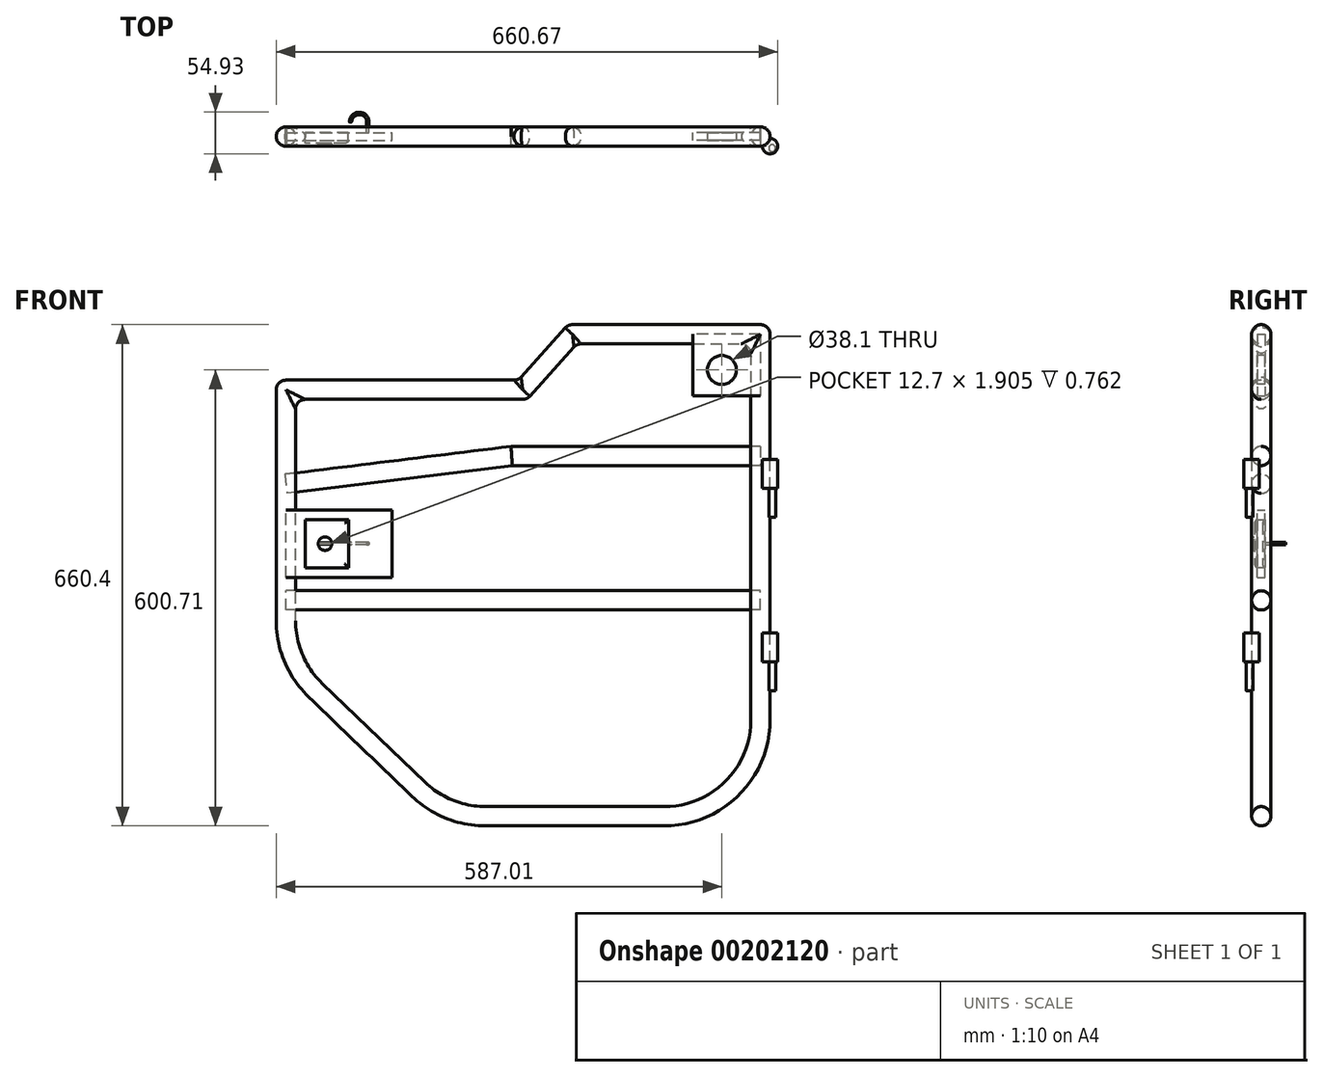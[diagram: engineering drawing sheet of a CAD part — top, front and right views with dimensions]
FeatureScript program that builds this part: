
annotation { "Feature Type Name" : "Feature", "Feature Type Description" : "" }
export const myFeature = defineFeature(function(context is Context, id is Id, definition is map)
    precondition{}
    {
        {
            var Q0;
            Q0=qCreatedBy(makeId("Front.planeOp"),FACE);
            var sketch = newSketch(context, id + "F0", { "sketchPlane" : qUnion([Q0])});
            skLineSegment(sketch, "E0", {"start": v(0, 0) * mm, "end": v(0, -508) * mm});
            skLineSegment(sketch, "E1", {"start": v(-127, -635) * mm, "end": v(-362.33, -635) * mm});
            skLineSegment(sketch, "E2", {"start": v(-450.34, -599.55) * mm, "end": v(-586.13, -469) * mm});
            skLineSegment(sketch, "E3", {"start": v(-625.11, -377.46) * mm, "end": v(-625.11, -73.1) * mm});
            skPoint(sketch, "E4.visualSharp", {"position": v(0, -635) * mm});
            skArc(sketch, "E4.filletArc", {"start": v(-127, -635) * mm, "mid": v(-37.2, -597.8) * mm, "end": v(0, -508) * mm});
            skPoint(sketch, "E5.visualSharp", {"position": v(-413.47, -635) * mm});
            skArc(sketch, "E5.filletArc", {"start": v(-450.34, -599.55) * mm, "mid": v(-409.77, -625.8) * mm, "end": v(-362.33, -635) * mm});
            skPoint(sketch, "E6.visualSharp", {"position": v(-625.11, -431.53) * mm});
            skArc(sketch, "E6.filletArc", {"start": v(-625.11, -377.46) * mm, "mid": v(-614.96, -427.2) * mm, "end": v(-586.13, -469) * mm});
            skLineSegment(sketch, "E7", {"start": v(0, 0) * mm, "end": v(-247.66, 0) * mm});
            skLineSegment(sketch, "E8", {"start": v(-247.66, 0) * mm, "end": v(-313.34, -73.1) * mm});
            skLineSegment(sketch, "E9", {"start": v(-313.34, -73.1) * mm, "end": v(-625.11, -73.1) * mm});
            skPoint(sketch, "E10.orphan", {"position": v(-625.11, 0) * mm});
            skSolve(sketch);
        }
        {
            var Q0;
            Q0=qCreatedBy(makeId("Top.planeOp"),FACE);
            var sketch = newSketch(context, id + "F1", { "sketchPlane" : qUnion([Q0])});
            skCircle(sketch, "E11", {"center": v(0, 0) * mm, "radius": 12.7 * mm});
            skSolve(sketch);
        }
        {
            var Q0;
            Q0=makeQuery(id+"F1.imprint","IMPRINT",FACE,{"disambiguationData":[TD([[makeQuery(id+"F1.imprint","IMPRINT",EDGE,{"derivedFrom":sQuery(id+"F1.wireOp",EDGE,"E11")}),1.0]])]});
            var Q1;
            Q1=sQuery(id+"F0.wireOp",EDGE,"E0");
            var Q2;
            Q2=sQuery(id+"F0.wireOp",EDGE,"E4.filletArc");
            var Q3;
            Q3=sQuery(id+"F0.wireOp",EDGE,"E1");
            var Q4;
            Q4=sQuery(id+"F0.wireOp",EDGE,"E5.filletArc");
            var Q5;
            Q5=sQuery(id+"F0.wireOp",EDGE,"E2");
            var Q6;
            Q6=sQuery(id+"F0.wireOp",EDGE,"E6.filletArc");
            var Q7;
            Q7=sQuery(id+"F0.wireOp",EDGE,"E3");
            var Q8;
            Q8=sQuery(id+"F0.wireOp",EDGE,"E7");
            var Q9;
            Q9=sQuery(id+"F0.wireOp",EDGE,"E8");
            var Q10;
            Q10=sQuery(id+"F0.wireOp",EDGE,"E9");
            sweep(context, id + "F2", {"profiles" : qUnion([Q0]), "path" : qUnion([Q1, Q2, Q3, Q4, Q5, Q6, Q7, Q8, Q9, Q10])});
        }
        {
            var Q0;
            Q0=qCreatedBy(makeId("Front.planeOp"),FACE);
            var sketch = newSketch(context, id + "F3", { "sketchPlane" : qUnion([Q0])});
            skLineSegment(sketch, "E12", {"start": v(0, -160.29) * mm, "end": v(-327.76, -160.29) * mm});
            skLineSegment(sketch, "E13", {"start": v(-327.76, -160.29) * mm, "end": v(-625.11, -197) * mm});
            skLineSegment(sketch, "E14", {"start": v(0, -350.6) * mm, "end": v(-625.11, -350.6) * mm});
            skSolve(sketch);
        }
        {
            var Q0;
            Q0=qCreatedBy(makeId("Right.planeOp"),FACE);
            var sketch = newSketch(context, id + "F4", { "sketchPlane" : qUnion([Q0])});
            skCircle(sketch, "E15", {"center": v(0, -160.29) * mm, "radius": 12.7 * mm});
            skCircle(sketch, "E16", {"center": v(0, -350.6) * mm, "radius": 12.7 * mm});
            skSolve(sketch);
        }
        {
            var Q0;
            Q0=makeQuery(id+"F4.imprint","IMPRINT",FACE,{"disambiguationData":[TD([[makeQuery(id+"F4.imprint","IMPRINT",EDGE,{"derivedFrom":sQuery(id+"F4.wireOp",EDGE,"E15")}),1.0]])]});
            var Q1;
            Q1=sQuery(id+"F3.wireOp",EDGE,"E12");
            var Q2;
            Q2=sQuery(id+"F3.wireOp",EDGE,"E13");
            sweep(context, id + "F5", {"profiles" : qUnion([Q0]), "path" : qUnion([Q1, Q2])});
        }
        {
            var Q0;
            Q0=makeQuery(id+"F4.imprint","IMPRINT",FACE,{"disambiguationData":[TD([[makeQuery(id+"F4.imprint","IMPRINT",EDGE,{"derivedFrom":sQuery(id+"F4.wireOp",EDGE,"E16")}),1.0]])]});
            var Q1;
            Q1=sQuery(id+"F3.wireOp",EDGE,"E14");
            sweep(context, id + "F6", {"profiles" : qUnion([Q0]), "path" : qUnion([Q1])});
        }
        {
            var Q0;
            Q0=qCreatedBy(makeId("Front.planeOp"),FACE);
            var sketch = newSketch(context, id + "F7", { "sketchPlane" : qUnion([Q0])});
            skLineSegment(sketch, "E17.bottom", {"start": v(-625.11, -320.3) * mm, "end": v(-485.41, -320.3) * mm});
            skLineSegment(sketch, "E17.top", {"start": v(-625.11, -231.4) * mm, "end": v(-485.41, -231.4) * mm});
            skLineSegment(sketch, "E17.left", {"start": v(-625.11, -320.3) * mm, "end": v(-625.11, -231.4) * mm});
            skLineSegment(sketch, "E17.right", {"start": v(-485.41, -320.3) * mm, "end": v(-485.41, -231.4) * mm});
            skSolve(sketch);
        }
        {
            var Q0;
            Q0 = qSketchRegion(id + "F7", true);
            extrude(context, id + "F8", {"entities" : qUnion([Q0]), "depth" : 5.08 * mm, "hasSecondDirection" : true, "secondDirectionOppositeDirection" : true, "secondDirectionDepth" : 5.08 * mm});
        }
        {
            var Q0;
            Q0=makeQuery(id+"F8.opExtrude","CAP_FACE",FACE,{"disambiguationData":[OSD([sQuery(id+"F7.wireOp",EDGE,"E17.bottom"),sQuery(id+"F7.wireOp",EDGE,"E17.top"),sQuery(id+"F7.wireOp",EDGE,"E17.left"),sQuery(id+"F7.wireOp",EDGE,"E17.right")])],"isStart":false});
            var sketch = newSketch(context, id + "F9", { "sketchPlane" : qUnion([Q0])});
            skLineSegment(sketch, "E18.bottom", {"start": v(-599.71, -244.1) * mm, "end": v(-542.56, -244.1) * mm});
            skLineSegment(sketch, "E18.top", {"start": v(-599.71, -307.6) * mm, "end": v(-542.56, -307.6) * mm});
            skLineSegment(sketch, "E18.left", {"start": v(-599.71, -244.1) * mm, "end": v(-599.71, -307.6) * mm});
            skLineSegment(sketch, "E18.right", {"start": v(-542.56, -244.1) * mm, "end": v(-542.56, -307.6) * mm});
            skSolve(sketch);
        }
        {
            var Q0;
            Q0 = qSketchRegion(id + "F9", true);
            extrude(context, id + "F10", {"entities" : qUnion([Q0]), "operationType" : NewBodyOperationType.ADD, "depth" : 3.8 * mm});
        }
        {
            var Q0;
            Q0=makeQuery(id+"F10.opExtrude","CAP_EDGE",EDGE,{"disambiguationData":[OSD([sQuery(id+"F9.wireOp",EDGE,"E18.bottom")])],"isStart":false});
            var Q1;
            Q1=makeQuery(id+"F10.opExtrude","CAP_EDGE",EDGE,{"disambiguationData":[OSD([sQuery(id+"F9.wireOp",EDGE,"E18.top")])],"isStart":false});
            var Q2;
            Q2=makeQuery(id+"F10.opExtrude","CAP_EDGE",EDGE,{"disambiguationData":[OSD([sQuery(id+"F9.wireOp",EDGE,"E18.right")])],"isStart":false});
            fillet(context, id + "F11", {"entities" : qUnion([Q0, Q1, Q2]), "radius" : 5.08 * mm, "tangentPropagation" : true, "allowEdgeOverflow" : false});
        }
        {
            var Q0;
            Q0=makeQuery(id+"F10.opExtrude","SWEPT_FACE",FACE,{"disambiguationData":[OSD([sQuery(id+"F9.wireOp",EDGE,"E18.left")])]});
            var sketch = newSketch(context, id + "F12", { "sketchPlane" : qUnion([Q0])});
            skLineSegment(sketch, "E19", {"start": v(-5.13, -244.78) * mm, "end": v(-5.13, -250.4) * mm});
            skLineSegment(sketch, "E20", {"start": v(8.9, -275.86) * mm, "end": v(-13.52, -275.86) * mm});
            skPoint(sketch, "E20.endSnap0", {"position": v(8.9, -275.86) * mm});
            skLineSegment(sketch, "E21", {"start": v(-5.13, -250.4) * mm, "end": v(-5.13, -275.86) * mm});
            skArc(sketch, "E22", {"start": v(-5.13, -244.78) * mm, "mid": v(-2.7, -246.31) * mm, "end": v(-1.76, -249.02) * mm});
            skLineSegment(sketch, "E23", {"start": v(-1.76, -249.02) * mm, "end": v(-1.76, -275.86) * mm});
            skLineSegment(sketch, "E24.MirrorCS", {"start": v(-1.76, -302.69) * mm, "end": v(-1.76, -275.86) * mm});
            skLineSegment(sketch, "E25.MirrorCS", {"start": v(-5.13, -301.31) * mm, "end": v(-5.13, -275.86) * mm});
            skLineSegment(sketch, "E26.MirrorCS", {"start": v(-5.13, -306.93) * mm, "end": v(-5.13, -301.31) * mm});
            skArc(sketch, "E27.MirrorCS", {"start": v(-5.13, -306.93) * mm, "mid": v(-2.7, -305.4) * mm, "end": v(-1.76, -302.69) * mm});
            skSolve(sketch);
        }
        {
            var Q0;
            Q0 = qSketchRegion(id + "F12", true);
            extrude(context, id + "F13", {"entities" : qUnion([Q0]), "operationType" : NewBodyOperationType.REMOVE, "oppositeDirection" : true, "depth" : 53.34 * mm});
        }
        {
            var Q0;
            Q0=makeQuery(id+"F8.opExtrude","CAP_FACE",FACE,{"disambiguationData":[OSD([sQuery(id+"F7.wireOp",EDGE,"E17.bottom"),sQuery(id+"F7.wireOp",EDGE,"E17.top"),sQuery(id+"F7.wireOp",EDGE,"E17.left"),sQuery(id+"F7.wireOp",EDGE,"E17.right")])],"isStart":true});
            var sketch = newSketch(context, id + "F14", { "sketchPlane" : qUnion([Q0])});
            skLineSegment(sketch, "E28", {"start": v(599.46, -244.36) * mm, "end": v(542.82, -244.36) * mm});
            skLineSegment(sketch, "E29", {"start": v(542.82, -244.36) * mm, "end": v(542.82, -307.35) * mm});
            skLineSegment(sketch, "E30", {"start": v(542.82, -307.35) * mm, "end": v(599.46, -307.35) * mm});
            skLineSegment(sketch, "E31", {"start": v(599.46, -307.35) * mm, "end": v(599.46, -244.36) * mm});
            skSolve(sketch);
        }
        {
            var Q0;
            Q0 = qSketchRegion(id + "F14", true);
            extrude(context, id + "F15", {"entities" : qUnion([Q0]), "operationType" : NewBodyOperationType.REMOVE, "oppositeDirection" : true, "depth" : 10.67 * mm});
        }
        {
            var Q0;
            Q0=makeQuery(id+"F8.opExtrude","SWEPT_FACE",FACE,{"disambiguationData":[OSD([sQuery(id+"F7.wireOp",EDGE,"E17.left")])]});
            cPlane(context, id + "F16", {"entities" : qUnion([Q0]), "cplaneType" : CPlaneType.OFFSET, "offset" : 107.95 * mm, "oppositeDirection" : true, "width" : 152.4 * mm, "height" : 152.4 * mm});
        }
        {
            var Q0;
            Q0=qCreatedBy(id+"F16.planeOp",FACE);
            var sketch = newSketch(context, id + "F17", { "sketchPlane" : qUnion([Q0])});
            skLineSegment(sketch, "E32", {"start": v(-5.08, -275.86) * mm, "end": v(-19.05, -275.86) * mm});
            skSolve(sketch);
        }
        {
            var Q0;
            Q0=makeQuery(id+"F8.opExtrude","SWEPT_FACE",FACE,{"disambiguationData":[OSD([sQuery(id+"F7.wireOp",EDGE,"E17.top")])]});
            cPlane(context, id + "F18", {"entities" : qUnion([Q0]), "cplaneType" : CPlaneType.OFFSET, "offset" : 44.45 * mm, "oppositeDirection" : true, "width" : 152.4 * mm, "height" : 152.4 * mm});
        }
        {
            var Q0;
            Q0=qCreatedBy(id+"F18.planeOp",FACE);
            var sketch = newSketch(context, id + "F19", { "sketchPlane" : qUnion([Q0])});
            skArc(sketch, "E33", {"start": v(-517.16, 19.05) * mm, "mid": v(-528.6, 30.48) * mm, "end": v(-540.02, 19.05) * mm});
            skSolve(sketch);
        }
        {
            var Q0;
            Q0=makeQuery(id+"F8.opExtrude","CAP_FACE",FACE,{"disambiguationData":[OSD([sQuery(id+"F7.wireOp",EDGE,"E17.bottom"),sQuery(id+"F7.wireOp",EDGE,"E17.top"),sQuery(id+"F7.wireOp",EDGE,"E17.left"),sQuery(id+"F7.wireOp",EDGE,"E17.right")])],"isStart":true});
            var sketch = newSketch(context, id + "F20", { "sketchPlane" : qUnion([Q0])});
            skLineSegment(sketch, "E34.bottom", {"start": v(518.75, -274.27) * mm, "end": v(515.58, -274.27) * mm});
            skLineSegment(sketch, "E34.top", {"start": v(518.75, -277.44) * mm, "end": v(515.58, -277.44) * mm});
            skLineSegment(sketch, "E34.left", {"start": v(518.75, -274.27) * mm, "end": v(518.75, -277.44) * mm});
            skLineSegment(sketch, "E34.right", {"start": v(515.58, -274.27) * mm, "end": v(515.58, -277.44) * mm});
            skPoint(sketch, "E34.middle", {"position": v(517.16, -275.86) * mm});
            skSolve(sketch);
        }
        {
            var Q0;
            Q0=makeQuery(id+"F20.imprint","IMPRINT",FACE,{"disambiguationData":[TD([[makeQuery(id+"F20.imprint","IMPRINT",EDGE,{"derivedFrom":sQuery(id+"F20.wireOp",EDGE,"E34.bottom")}),1.0]])]});
            var Q1;
            Q1=sQuery(id+"F17.wireOp",EDGE,"E32");
            var Q2;
            Q2=sQuery(id+"F19.wireOp",EDGE,"E33");
            sweep(context, id + "F21", {"operationType" : NewBodyOperationType.ADD, "profiles" : qUnion([Q0]), "path" : qUnion([Q1, Q2])});
        }
        {
            var Q0;
            Q0=makeQuery(id+"F21.opSweep","CAP_EDGE",EDGE,{"disambiguationData":[OSD([sQuery(id+"F19.wireOp",VERTEX,"E33.end"),sQuery(id+"F20.wireOp",EDGE,"E34.right")])],"isStart":false});
            var Q1;
            Q1=makeQuery(id+"F21.opSweep","CAP_EDGE",EDGE,{"disambiguationData":[OSD([sQuery(id+"F19.wireOp",VERTEX,"E33.end"),sQuery(id+"F20.wireOp",EDGE,"E34.left")])],"isStart":false});
            var Q2;
            Q2=makeQuery(id+"F21.opSweep","CAP_EDGE",EDGE,{"disambiguationData":[OSD([sQuery(id+"F19.wireOp",VERTEX,"E33.end"),sQuery(id+"F20.wireOp",EDGE,"E34.bottom")])],"isStart":false});
            var Q3;
            Q3=makeQuery(id+"F21.opSweep","CAP_EDGE",EDGE,{"disambiguationData":[OSD([sQuery(id+"F19.wireOp",VERTEX,"E33.end"),sQuery(id+"F20.wireOp",EDGE,"E34.top")])],"isStart":false});
            fillet(context, id + "F22", {"entities" : qUnion([Q0, Q1, Q2, Q3]), "radius" : 0.5 * mm, "tangentPropagation" : true, "allowEdgeOverflow" : false});
        }
        {
            var Q0;
            Q0=makeQuery(id+"F10.opExtrude","CAP_FACE",FACE,{"disambiguationData":[OSD([sQuery(id+"F9.wireOp",EDGE,"E18.bottom"),sQuery(id+"F9.wireOp",EDGE,"E18.top"),sQuery(id+"F9.wireOp",EDGE,"E18.left"),sQuery(id+"F9.wireOp",EDGE,"E18.right")])],"isStart":false});
            var sketch = newSketch(context, id + "F23", { "sketchPlane" : qUnion([Q0])});
            skCircle(sketch, "E35", {"center": v(-573.6, -275.86) * mm, "radius": 8.9 * mm});
            skPoint(sketch, "E35.centerSnap0", {"position": v(-547.48, -275.86) * mm});
            skPoint(sketch, "E35.centerSnap1", {"position": v(-573.6, -249.02) * mm});
            skSolve(sketch);
        }
        {
            var Q0;
            Q0 = qSketchRegion(id + "F23", true);
            extrude(context, id + "F24", {"entities" : qUnion([Q0]), "operationType" : NewBodyOperationType.ADD, "depth" : 2.54 * mm});
        }
        {
            var Q0;
            Q0=makeQuery(id+"F24.opExtrude","CAP_EDGE",EDGE,{"disambiguationData":[OSD([sQuery(id+"F23.wireOp",EDGE,"E35")])],"isStart":false});
            fillet(context, id + "F25", {"entities" : qUnion([Q0]), "radius" : 1.27 * mm, "tangentPropagation" : true, "allowEdgeOverflow" : false});
        }
        {
            var Q0;
            Q0=makeQuery(id+"F24.opExtrude","CAP_FACE",FACE,{"disambiguationData":[OSD([sQuery(id+"F23.wireOp",EDGE,"E35")])],"isStart":false});
            var sketch = newSketch(context, id + "F26", { "sketchPlane" : qUnion([Q0])});
            skLineSegment(sketch, "E36.bottom", {"start": v(-567.25, -276.8) * mm, "end": v(-579.95, -276.8) * mm});
            skLineSegment(sketch, "E36.top", {"start": v(-567.25, -274.9) * mm, "end": v(-579.95, -274.9) * mm});
            skLineSegment(sketch, "E36.left", {"start": v(-567.25, -276.8) * mm, "end": v(-567.25, -274.9) * mm});
            skLineSegment(sketch, "E36.right", {"start": v(-579.95, -276.8) * mm, "end": v(-579.95, -274.9) * mm});
            skPoint(sketch, "E36.middle", {"position": v(-573.6, -275.86) * mm});
            skSolve(sketch);
        }
        {
            var Q0;
            Q0 = qSketchRegion(id + "F26", true);
            extrude(context, id + "F27", {"entities" : qUnion([Q0]), "operationType" : NewBodyOperationType.REMOVE, "oppositeDirection" : true, "depth" : 0.76 * mm});
        }
        {
            var Q0;
            Q0=qCreatedBy(makeId("Front.planeOp"),FACE);
            var sketch = newSketch(context, id + "F28", { "sketchPlane" : qUnion([Q0])});
            skLineSegment(sketch, "E37.bottom", {"start": v(0, 0) * mm, "end": v(-88.9, 0) * mm});
            skLineSegment(sketch, "E37.top", {"start": v(0, -81.28) * mm, "end": v(-88.9, -81.28) * mm});
            skLineSegment(sketch, "E37.left", {"start": v(0, 0) * mm, "end": v(0, -81.28) * mm});
            skLineSegment(sketch, "E37.right", {"start": v(-88.9, 0) * mm, "end": v(-88.9, -81.28) * mm});
            skSolve(sketch);
        }
        {
            var Q0;
            Q0 = qSketchRegion(id + "F28", true);
            extrude(context, id + "F29", {"entities" : qUnion([Q0]), "depth" : 5.08 * mm, "hasSecondDirection" : true, "secondDirectionOppositeDirection" : true, "secondDirectionDepth" : 5.08 * mm});
        }
        {
            var Q0;
            Q0=makeQuery(id+"F29.opExtrude","CAP_FACE",FACE,{"disambiguationData":[OSD([sQuery(id+"F28.wireOp",EDGE,"E37.bottom"),sQuery(id+"F28.wireOp",EDGE,"E37.top"),sQuery(id+"F28.wireOp",EDGE,"E37.left"),sQuery(id+"F28.wireOp",EDGE,"E37.right")])],"isStart":false});
            var sketch = newSketch(context, id + "F30", { "sketchPlane" : qUnion([Q0])});
            skCircle(sketch, "E38", {"center": v(-50.8, -47) * mm, "radius": 19.05 * mm});
            skPoint(sketch, "E38.centerSnap0", {"position": v(4.45, -47) * mm});
            skPoint(sketch, "E38.centerSnap1", {"position": v(-50.8, 3.08) * mm});
            skSolve(sketch);
        }
        {
            var Q0;
            Q0 = qSketchRegion(id + "F30", true);
            extrude(context, id + "F31", {"entities" : qUnion([Q0]), "operationType" : NewBodyOperationType.REMOVE, "oppositeDirection" : true, "depth" : 10.16 * mm});
        }
        {
            var Q0;
            Q0=qCreatedBy(makeId("Top.planeOp"),FACE);
            cPlane(context, id + "F32", {"entities" : qUnion([Q0]), "cplaneType" : CPlaneType.OFFSET, "offset" : 165.1 * mm, "oppositeDirection" : true, "width" : 152.4 * mm, "height" : 152.4 * mm});
        }
        {
            var Q0;
            Q0=qCreatedBy(id+"F32.planeOp",FACE);
            var sketch = newSketch(context, id + "F33", { "sketchPlane" : qUnion([Q0])});
            skCircle(sketch, "E39", {"center": v(12.7, -12.7) * mm, "radius": 10.16 * mm});
            skSolve(sketch);
        }
        {
            var Q0;
            Q0 = qSketchRegion(id + "F33", true);
            extrude(context, id + "F34", {"entities" : qUnion([Q0]), "operationType" : NewBodyOperationType.ADD, "oppositeDirection" : true, "depth" : 38.1 * mm});
        }
        {
            var Q0;
            Q0=makeQuery(id+"F34.opExtrude","CAP_FACE",FACE,{"disambiguationData":[OSD([sQuery(id+"F33.wireOp",EDGE,"E39")])],"isStart":false});
            var sketch = newSketch(context, id + "F35", { "sketchPlane" : qUnion([Q0])});
            skCircle(sketch, "E40", {"center": v(15.37, 15.37) * mm, "radius": 4.45 * mm});
            skSolve(sketch);
        }
        {
            var Q0;
            Q0=makeQuery(id+"F35.imprint","IMPRINT",FACE,{"disambiguationData":[TD([[makeQuery(id+"F35.imprint","IMPRINT",EDGE,{"derivedFrom":sQuery(id+"F35.wireOp",EDGE,"E40")}),1.0]])]});
            extrude(context, id + "F36", {"entities" : qUnion([Q0]), "operationType" : NewBodyOperationType.ADD, "depth" : 38.1 * mm});
        }
        {
            var Q0;
            Q0=qCreatedBy(id+"F32.planeOp",FACE);
            cPlane(context, id + "F37", {"entities" : qUnion([Q0]), "cplaneType" : CPlaneType.OFFSET, "offset" : 228.6 * mm, "oppositeDirection" : true, "width" : 152.4 * mm, "height" : 152.4 * mm});
        }
        {
            var Q0;
            Q0=qCreatedBy(id+"F37.planeOp",FACE);
            var sketch = newSketch(context, id + "F38", { "sketchPlane" : qUnion([Q0])});
            skCircle(sketch, "E41", {"center": v(12.7, -12.7) * mm, "radius": 10.16 * mm});
            skSolve(sketch);
        }
        {
            var Q0;
            Q0 = qSketchRegion(id + "F38", true);
            extrude(context, id + "F39", {"entities" : qUnion([Q0]), "operationType" : NewBodyOperationType.ADD, "oppositeDirection" : true, "depth" : 38.1 * mm});
        }
        {
            var Q0;
            Q0=makeQuery(id+"F39.opExtrude","CAP_FACE",FACE,{"disambiguationData":[OSD([sQuery(id+"F38.wireOp",EDGE,"E41")])],"isStart":false});
            var sketch = newSketch(context, id + "F40", { "sketchPlane" : qUnion([Q0])});
            skCircle(sketch, "E42", {"center": v(15.37, 15.37) * mm, "radius": 4.45 * mm});
            skSolve(sketch);
        }
        {
            var Q0;
            Q0 = qSketchRegion(id + "F40", true);
            extrude(context, id + "F41", {"entities" : qUnion([Q0]), "operationType" : NewBodyOperationType.ADD, "depth" : 38.1 * mm});
        }
        {
            var Q0;
            Q0=makeQuery(id+"F2.opSweep","MID_CAP_EDGE",EDGE,{"disambiguationData":[OSD([sQuery(id+"F0.wireOp",VERTEX,"E9.end"),sQuery(id+"F1.wireOp",EDGE,"E11")])],"capPos":7.0});
            var Q1;
            Q1=makeQuery(id+"F2.opSweep","MID_CAP_EDGE",EDGE,{"disambiguationData":[OSD([sQuery(id+"F0.wireOp",VERTEX,"E9.start"),sQuery(id+"F1.wireOp",EDGE,"E11")])],"capPos":8.0});
            var Q2;
            Q2=makeQuery(id+"F2.opSweep","MID_CAP_EDGE",EDGE,{"disambiguationData":[OSD([sQuery(id+"F0.wireOp",VERTEX,"E8.start"),sQuery(id+"F1.wireOp",EDGE,"E11")])],"capPos":9.0});
            var Q3;
            Q3=makeQuery(id+"F2.opSweep","CAP_EDGE",EDGE,{"disambiguationData":[OSD([sQuery(id+"F0.wireOp",VERTEX,"E7.start"),sQuery(id+"F1.wireOp",EDGE,"E11")])],"isStart":true});
            fillet(context, id + "F42", {"entities" : qUnion([Q0, Q1, Q2, Q3]), "radius" : 12.7 * mm, "tangentPropagation" : true, "allowEdgeOverflow" : false});
        }
    });
